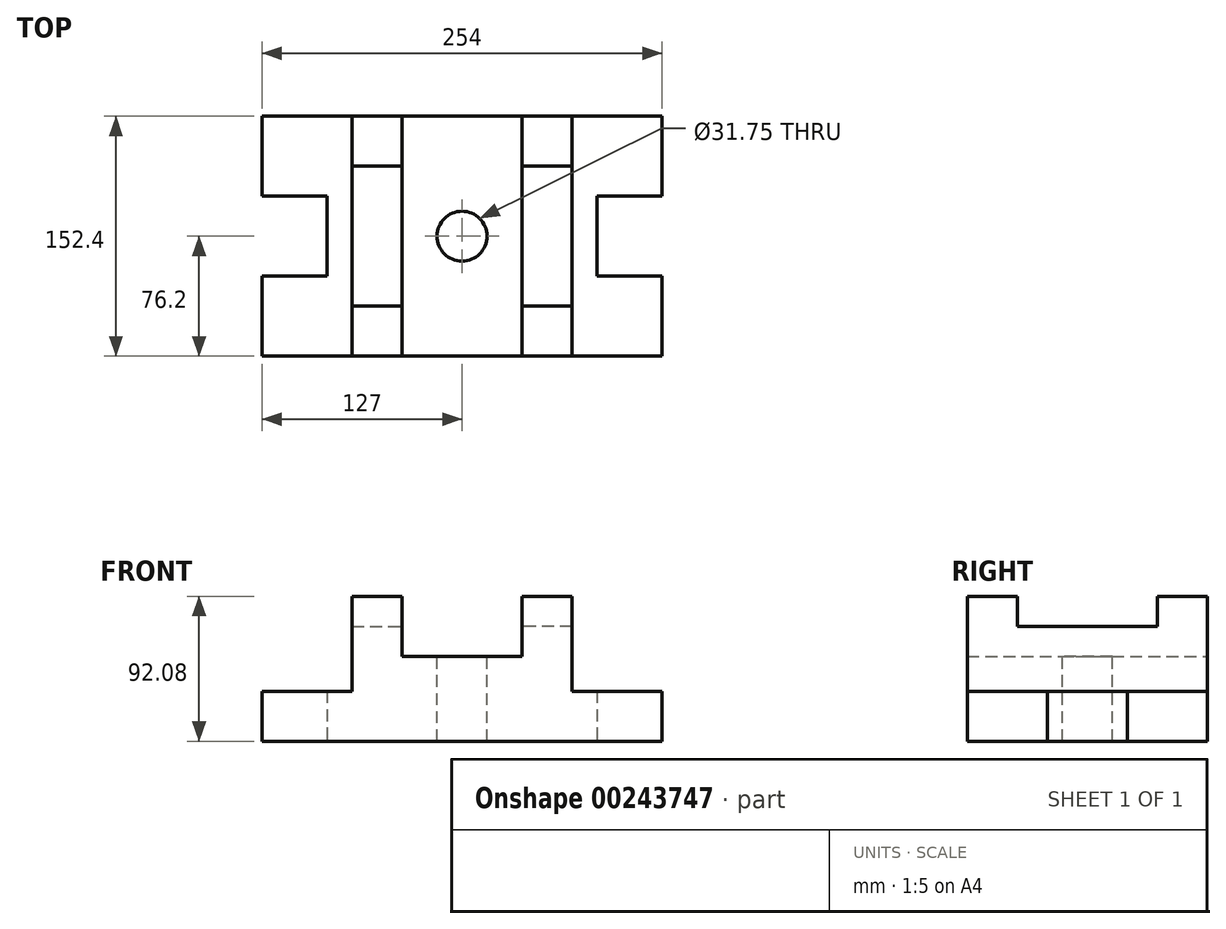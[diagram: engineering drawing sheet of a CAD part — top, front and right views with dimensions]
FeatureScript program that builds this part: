
annotation { "Feature Type Name" : "Feature", "Feature Type Description" : "" }
export const myFeature = defineFeature(function(context is Context, id is Id, definition is map)
    precondition{}
    {
        {
            var Q0;
            Q0=qCreatedBy(makeId("Front.planeOp"),FACE);
            var sketch = newSketch(context, id + "F0", { "sketchPlane" : qUnion([Q0])});
            skLineSegment(sketch, "E0.bottom", {"start": v(19.05, 26.99) * mm, "end": v(-19.05, 26.99) * mm});
            skLineSegment(sketch, "E0.top", {"start": v(19.05, -26.99) * mm, "end": v(-19.05, -26.99) * mm});
            skLineSegment(sketch, "E0.left", {"start": v(19.05, 26.99) * mm, "end": v(19.05, -26.99) * mm});
            skLineSegment(sketch, "E0.right", {"start": v(-19.05, 26.99) * mm, "end": v(-19.05, -26.99) * mm});
            skPoint(sketch, "E0.middle", {"position": v(0, 0) * mm});
            skLineSegment(sketch, "E1.bottom", {"start": v(19.05, -26.99) * mm, "end": v(50.8, -26.99) * mm});
            skLineSegment(sketch, "E1.top", {"start": v(19.05, 65.09) * mm, "end": v(50.8, 65.09) * mm});
            skLineSegment(sketch, "E1.left", {"start": v(19.05, -26.99) * mm, "end": v(19.05, 65.09) * mm});
            skLineSegment(sketch, "E1.right", {"start": v(50.8, -26.99) * mm, "end": v(50.8, 65.09) * mm});
            skLineSegment(sketch, "E2.bottom", {"start": v(50.8, -26.99) * mm, "end": v(107.95, -26.99) * mm});
            skLineSegment(sketch, "E2.top", {"start": v(50.8, 4.76) * mm, "end": v(107.95, 4.76) * mm});
            skLineSegment(sketch, "E2.left", {"start": v(50.8, -26.99) * mm, "end": v(50.8, 4.76) * mm});
            skLineSegment(sketch, "E2.right", {"start": v(107.95, -26.99) * mm, "end": v(107.95, 4.76) * mm});
            skLineSegment(sketch, "E3.top", {"start": v(19.05, 46.04) * mm, "end": v(50.8, 46.04) * mm});
            skLineSegment(sketch, "E3.left", {"start": v(19.05, 65.09) * mm, "end": v(19.05, 46.04) * mm});
            skLineSegment(sketch, "E3.right", {"start": v(50.8, 65.09) * mm, "end": v(50.8, 46.04) * mm});
            skSolve(sketch);
        }
        {
            var Q0;
            {var subQ0=sQuery(id+"F0.wireOp",EDGE,"E0.bottom");Q0=makeQuery(id+"F0.imprint","IMPRINT",FACE,{"disambiguationData":[TD([[makeQuery(id+"F0.imprint","IMPRINT",EDGE,{"derivedFrom":subQ0}),1.0]])]});}
            var Q1;
            {var subQ3=sQuery(id+"F0.wireOp",EDGE,"E1.bottom");Q1=makeQuery(id+"F0.imprint","IMPRINT",FACE,{"disambiguationData":[TD([[makeQuery(id+"F0.imprint","IMPRINT",EDGE,{"derivedFrom":subQ3}),1.0]])]});}
            var Q2;
            Q2=makeQuery(id+"F0.imprint","IMPRINT",FACE,{"disambiguationData":[TD([[makeQuery(id+"F0.imprint","IMPRINT",EDGE,{"derivedFrom":sQuery(id+"F0.wireOp",EDGE,"E2.bottom")}),1.0]])]});
            var Q3;
            Q3=makeQuery(id+"F0.imprint","IMPRINT",FACE,{"disambiguationData":[TD([[makeQuery(id+"F0.imprint","IMPRINT",EDGE,{"derivedFrom":sQuery(id+"F0.wireOp",EDGE,"E1.top")}),-1.0]])]});
            extrude(context, id + "F1", {"entities" : qUnion([Q0, Q1, Q2, Q3]), "endBound" : BoundingType.SYMMETRIC, "depth" : 76.2 * mm});
        }
        {
            var Q0;
            Q0=makeQuery(id+"F1.opExtrude","CAP_FACE",FACE,{"disambiguationData":[OSD([sQuery(id+"F0.wireOp",EDGE,"E0.bottom"),sQuery(id+"F0.wireOp",EDGE,"E0.top"),sQuery(id+"F0.wireOp",EDGE,"E0.right"),sQuery(id+"F0.wireOp",EDGE,"E1.bottom"),sQuery(id+"F0.wireOp",EDGE,"E1.left"),sQuery(id+"F0.wireOp",EDGE,"E1.right"),sQuery(id+"F0.wireOp",EDGE,"E2.bottom"),sQuery(id+"F0.wireOp",EDGE,"E2.top"),sQuery(id+"F0.wireOp",EDGE,"E2.right"),sQuery(id+"F0.wireOp",EDGE,"E1.top"),sQuery(id+"F0.wireOp",EDGE,"E3.left"),sQuery(id+"F0.wireOp",EDGE,"E3.right")])],"isStart":true});
            var sketch = newSketch(context, id + "F2", { "sketchPlane" : qUnion([Q0])});
            skLineSegment(sketch, "E4.bottom", {"start": v(-50.8, 65.09) * mm, "end": v(-19.05, 65.09) * mm});
            skLineSegment(sketch, "E4.top", {"start": v(-50.8, 46.04) * mm, "end": v(-19.05, 46.04) * mm});
            skLineSegment(sketch, "E4.left", {"start": v(-50.8, 65.09) * mm, "end": v(-50.8, 46.04) * mm});
            skLineSegment(sketch, "E4.right", {"start": v(-19.05, 65.09) * mm, "end": v(-19.05, 46.04) * mm});
            skSolve(sketch);
        }
        {
            var Q0;
            Q0=makeQuery(id+"F2.imprint","IMPRINT",FACE,{"disambiguationData":[TD([[makeQuery(id+"F2.imprint","IMPRINT",EDGE,{"derivedFrom":sQuery(id+"F2.wireOp",EDGE,"E4.bottom")}),1.0]])]});
            extrude(context, id + "F3", {"entities" : qUnion([Q0]), "operationType" : NewBodyOperationType.REMOVE, "oppositeDirection" : true, "depth" : 44.45 * mm});
        }
        {
            var Q0;
            Q0=makeQuery(id+"F1.opExtrude","CAP_FACE",FACE,{"disambiguationData":[OSD([sQuery(id+"F0.wireOp",EDGE,"E0.bottom"),sQuery(id+"F0.wireOp",EDGE,"E0.top"),sQuery(id+"F0.wireOp",EDGE,"E0.right"),sQuery(id+"F0.wireOp",EDGE,"E1.bottom"),sQuery(id+"F0.wireOp",EDGE,"E1.left"),sQuery(id+"F0.wireOp",EDGE,"E1.right"),sQuery(id+"F0.wireOp",EDGE,"E2.bottom"),sQuery(id+"F0.wireOp",EDGE,"E2.top"),sQuery(id+"F0.wireOp",EDGE,"E2.right"),sQuery(id+"F0.wireOp",EDGE,"E1.top"),sQuery(id+"F0.wireOp",EDGE,"E3.left"),sQuery(id+"F0.wireOp",EDGE,"E3.right")])],"isStart":true});
            var sketch = newSketch(context, id + "F4", { "sketchPlane" : qUnion([Q0])});
            skLineSegment(sketch, "E5.bottom", {"start": v(-107.95, 4.76) * mm, "end": v(-66.68, 4.76) * mm});
            skLineSegment(sketch, "E5.top", {"start": v(-107.95, -26.99) * mm, "end": v(-66.68, -26.99) * mm});
            skLineSegment(sketch, "E5.left", {"start": v(-107.95, 4.76) * mm, "end": v(-107.95, -26.99) * mm});
            skLineSegment(sketch, "E5.right", {"start": v(-66.68, 4.76) * mm, "end": v(-66.68, -26.99) * mm});
            skSolve(sketch);
        }
        {
            var Q0;
            Q0 = qSketchRegion(id + "F4", true);
            extrude(context, id + "F5", {"entities" : qUnion([Q0]), "operationType" : NewBodyOperationType.REMOVE, "oppositeDirection" : true, "depth" : 25.4 * mm});
        }
        {
            var Q0;
            Q0=makeQuery(id+"F1.opExtrude","SWEPT_BODY",BODY,{"disambiguationData":[OSD([sQuery(id+"F0.wireOp",EDGE,"E0.bottom"),sQuery(id+"F0.wireOp",EDGE,"E0.top"),sQuery(id+"F0.wireOp",EDGE,"E0.right"),sQuery(id+"F0.wireOp",EDGE,"E1.bottom"),sQuery(id+"F0.wireOp",EDGE,"E1.left"),sQuery(id+"F0.wireOp",EDGE,"E1.right"),sQuery(id+"F0.wireOp",EDGE,"E2.bottom"),sQuery(id+"F0.wireOp",EDGE,"E2.top"),sQuery(id+"F0.wireOp",EDGE,"E2.right"),sQuery(id+"F0.wireOp",EDGE,"E1.top"),sQuery(id+"F0.wireOp",EDGE,"E3.left"),sQuery(id+"F0.wireOp",EDGE,"E3.right")])]});
            var Q1;
            Q1=makeQuery(id+"F1.opExtrude","CAP_FACE",FACE,{"disambiguationData":[OSD([sQuery(id+"F0.wireOp",EDGE,"E0.bottom"),sQuery(id+"F0.wireOp",EDGE,"E0.top"),sQuery(id+"F0.wireOp",EDGE,"E0.right"),sQuery(id+"F0.wireOp",EDGE,"E1.bottom"),sQuery(id+"F0.wireOp",EDGE,"E1.left"),sQuery(id+"F0.wireOp",EDGE,"E1.right"),sQuery(id+"F0.wireOp",EDGE,"E2.bottom"),sQuery(id+"F0.wireOp",EDGE,"E2.top"),sQuery(id+"F0.wireOp",EDGE,"E2.right"),sQuery(id+"F0.wireOp",EDGE,"E1.top"),sQuery(id+"F0.wireOp",EDGE,"E3.left"),sQuery(id+"F0.wireOp",EDGE,"E3.right")])],"isStart":true});
            mirror(context, id + "F6", {"operationType" : NewBodyOperationType.ADD, "entities" : qUnion([Q0]), "mirrorPlane" : qUnion([Q1])});
        }
        {
            var Q0;
            Q0=makeQuery(id+"F1.opExtrude","SWEPT_BODY",BODY,{"disambiguationData":[OSD([sQuery(id+"F0.wireOp",EDGE,"E0.bottom"),sQuery(id+"F0.wireOp",EDGE,"E0.top"),sQuery(id+"F0.wireOp",EDGE,"E0.right"),sQuery(id+"F0.wireOp",EDGE,"E1.bottom"),sQuery(id+"F0.wireOp",EDGE,"E1.left"),sQuery(id+"F0.wireOp",EDGE,"E1.right"),sQuery(id+"F0.wireOp",EDGE,"E2.bottom"),sQuery(id+"F0.wireOp",EDGE,"E2.top"),sQuery(id+"F0.wireOp",EDGE,"E2.right"),sQuery(id+"F0.wireOp",EDGE,"E1.top"),sQuery(id+"F0.wireOp",EDGE,"E3.left"),sQuery(id+"F0.wireOp",EDGE,"E3.right")])]});
            var Q1;
            {var subQ0=makeQuery(id+"F1.opExtrude","SWEPT_FACE",FACE,{"disambiguationData":[OSD([sQuery(id+"F0.wireOp",EDGE,"E0.right")])]});Q1=makeQuery(id+"F6.boolean.opBoolean","MERGE",FACE,{"derivedFrom":[subQ0,makeQuery(id+"F6.opPattern","COPY",FACE,{"derivedFrom":subQ0,"instanceName":"1"})]});}
            mirror(context, id + "F7", {"operationType" : NewBodyOperationType.ADD, "entities" : qUnion([Q0]), "mirrorPlane" : qUnion([Q1])});
        }
        {
            var Q0;
            {var subQ0=makeQuery(id+"F1.opExtrude","SWEPT_FACE",FACE,{"disambiguationData":[OSD([sQuery(id+"F0.wireOp",EDGE,"E0.bottom")])]});var subQ1=makeQuery(id+"F6.boolean.opBoolean","MERGE",FACE,{"derivedFrom":[subQ0,makeQuery(id+"F6.opPattern","COPY",FACE,{"derivedFrom":subQ0,"instanceName":"1"})]});Q0=makeQuery(id+"F7.boolean.opBoolean","MERGE",FACE,{"derivedFrom":[subQ1,makeQuery(id+"F7.opPattern","COPY",FACE,{"derivedFrom":subQ1,"instanceName":"1"})]});}
            var sketch = newSketch(context, id + "F8", { "sketchPlane" : qUnion([Q0])});
            skCircle(sketch, "E6", {"center": v(-19.05, 38.1) * mm, "radius": 15.88 * mm});
            skSolve(sketch);
        }
        {
            var Q0;
            Q0=makeQuery(id+"F8.imprint","IMPRINT",FACE,{"disambiguationData":[TD([[makeQuery(id+"F8.imprint","IMPRINT",EDGE,{"derivedFrom":sQuery(id+"F8.wireOp",EDGE,"E6")}),1.0]])]});
            extrude(context, id + "F9", {"entities" : qUnion([Q0]), "operationType" : NewBodyOperationType.REMOVE, "endBound" : BoundingType.THROUGH_ALL, "oppositeDirection" : true, "depth" : 25.4 * mm});
        }
    });
